# Revit family: Sno-Safe Snow Guards Original UV Resistant Polycarbonate
name_source: partatom
category: Generic Models
revit_build: Autodesk Revit 2018 (Build: 20190510_1515(x64)
units: mm (PartAtom-declared; Revit-internal decimal feet)

## family parameters
Always vertical = No
Can host rebar = No
Cut with Voids When Loaded = No
Host = Roof
Part Type = Normal
Room Calculation Point = No
Round Connector Dimension = Use Diameter
Shared = No

## types (1)
- Sno-Safe Snow Guards Original UV Resistant Polycarbonate
    Colors = 14) Bone White
    Link for requesting a custom layout = https://nam11.safelinks.protection.outlook.com
    Manufacturer = Sno-Safe Snow Guards
    Material = UV Resistant Polycarbonate
    Methods of attachment = Adhesive or Roofing screws with sealant
    Model = Original Polycarbonate Snow Guards
    Suggested Adhesive = Surebond SB-190
    Website = https://nam11.safelinks.protection.outlook.com

## geometry (parser evidence)
native form markers: Sweep x5
no freeform markers — native parametric forms only
